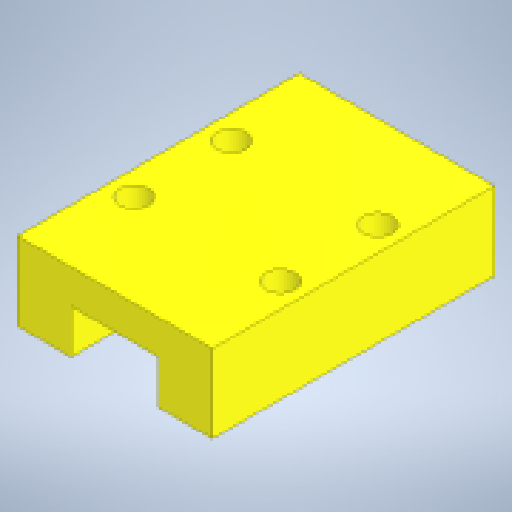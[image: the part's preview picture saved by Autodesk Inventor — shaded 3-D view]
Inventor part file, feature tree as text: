
AUTODESK INVENTOR PART (.ipt)
format: ipt  version: 2024 (Build 280153000, 153)  size: 154,624 bytes
history: native  units: in
note: dims shown in document units (in); Inventor stores cm internally (conversion verified against a paired STEP export)
features: extrude x2, sketch x2
ambient origin geometry x8: Origin, YZ Plane, XZ Plane, XY Plane, X Axis, Y Axis, Z Axis, Center Point
bodies: Solid1 (feature_tree)
feature tree (4):
  extrude  "Extrusion1"  Depth=0.315in
  extrude  "Extrusion2"  Depth=0.3543in
  sketch  "Sketch1"  dims[d0=0.7874in d1=0.315in]
  sketch  "Sketch2"  dims[d2=0.1772in d3=0.3543in d4=0.2165in d5=1.1378in d6=0.0in d7=0.1181in d8=0.1181in d9=0.1181in d10=0.1181in d11=0.372in d12=0.372in d13=0.3937in d14=0.3937in d15=0.0984in d16=0.0984in d18=0.0984in d19=0.0984in d20=0.315in d21=0.0in]
